# Revit family: Magnuson-Receptacles-Trosa+
name_source: partatom
category: Furniture
units: mm (PartAtom-declared; Revit-internal decimal feet)

## family parameters
Always vertical = Yes
Cut with Voids When Loaded = No
OmniClass Number = 23.40.20.00
OmniClass Title = General Furniture and Specialties
Room Calculation Point = No
Shared = No
Work Plane-Based = No

## types (1)
- TRO-1818L
    Acrylic Finish = MAG - Acrylic, Clear
    Assembly Code = E2020200
    Default Elevation = 0"
    Depth = 18"
    Description = Painted steel 42 gallon body waste receptacle with front access door, internal rigid liner and adjustable glides.
    Door Finish = MAG - Steel Painted
    Frame Finish = MAG - Steel Painted
    Glides Finish = MAG - Plastic Black
    Height = 40"
    Keynote = 12500
    Liner Finish = MAG - Plastic Black
    Lock Finish = MAG - Aluminum Black
    Low Emitting Finish = Yes
    Low Emitting Material = Yes
    Manufacturer = Magnuson Group
    Model = TRO-1818L
    Percentage of Recycled Content = 0
    Product Documentation Link = https://magnusongroup.com
    Revit Model Built By = https://servex-us.com
    Salvage or Reuse = Yes
    Signage Finish = MAG - Steel Painted
    Top Finish = MAG - Steel Painted
    Type Comments = Waste Receptacles
    URL = https://magnusongroup.com
    Width = 18"

## geometry (parser evidence)
native form markers: Sweep x4
no freeform markers — native parametric forms only
